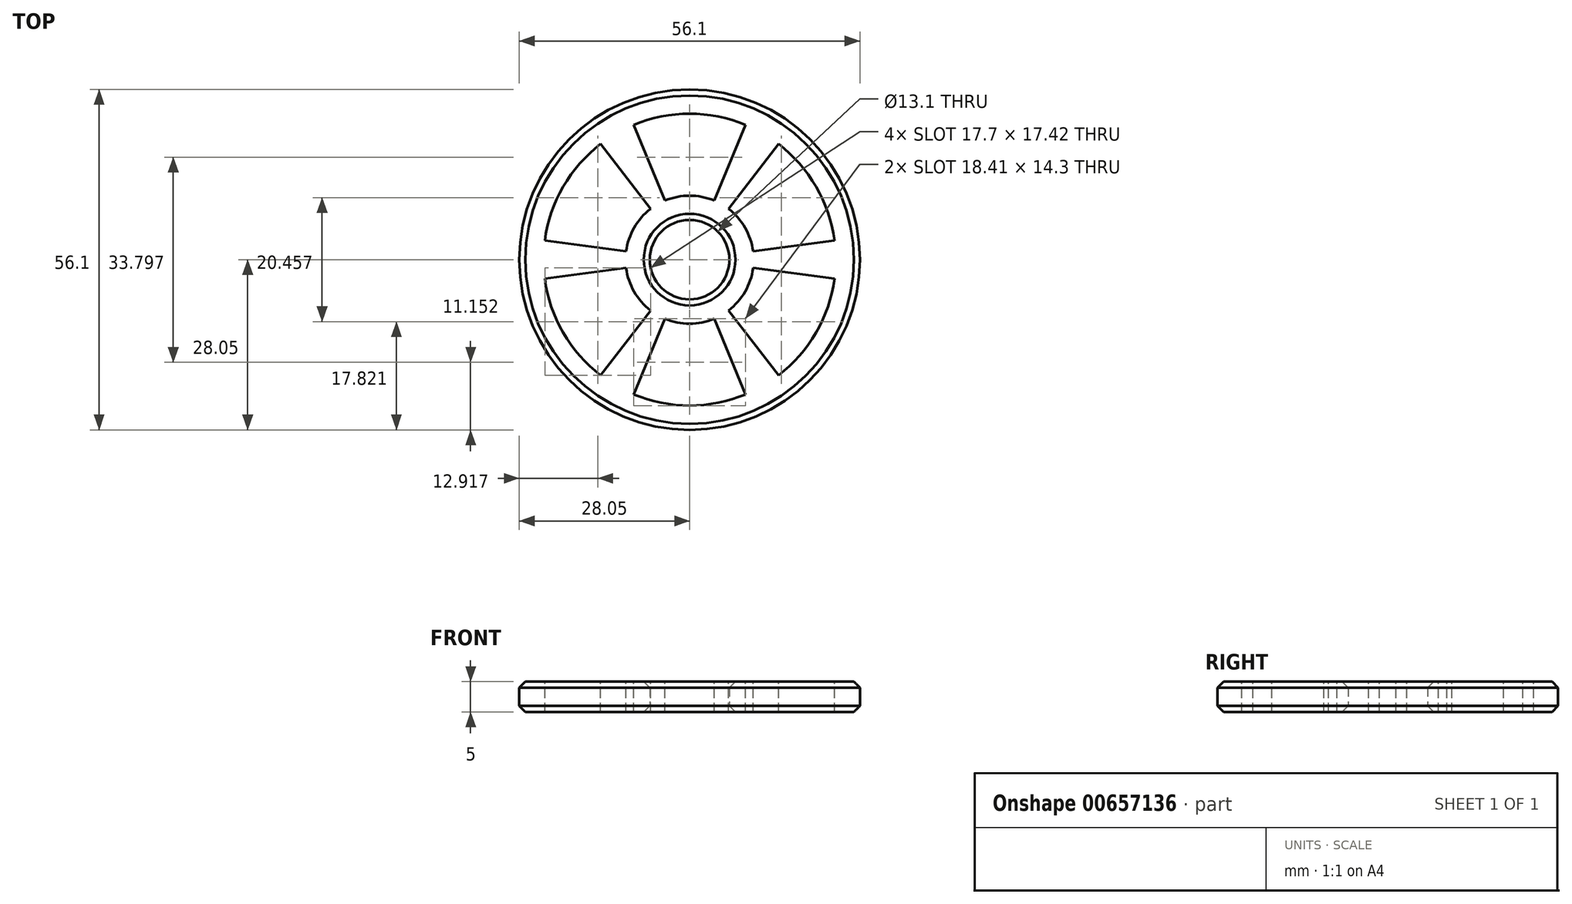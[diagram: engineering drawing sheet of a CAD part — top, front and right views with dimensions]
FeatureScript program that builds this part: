
annotation { "Feature Type Name" : "Feature", "Feature Type Description" : "" }
export const myFeature = defineFeature(function(context is Context, id is Id, definition is map)
    precondition{}
    {
        {
            assignVariable(context, id + "F0", {"name" : "e", "anyValue" : 5});
        }
        {
            var Q0;
            Q0=qCreatedBy(makeId("Top.planeOp"),FACE);
            var sketch = newSketch(context, id + "F1", { "sketchPlane" : qUnion([Q0])});
            skCircle(sketch, "E0", {"center": v(0, 0) * mm, "radius": 28.05 * mm});
            skCircle(sketch, "E1", {"center": v(0, 0) * mm, "radius": 6.55 * mm});
            skSolve(sketch);
        }
        {
            var Q0;
            Q0=makeQuery(id+"F1.imprint","IMPRINT",FACE,{"disambiguationData":[TD([[makeQuery(id+"F1.imprint","IMPRINT",EDGE,{"derivedFrom":sQuery(id+"F1.wireOp",EDGE,"E0")}),1.0]])]});
            extrude(context, id + "F2", {"entities" : qUnion([Q0]), "depth" : (getVariable(context, 'e')) * mm, "offsetDistance" : 25 * mm});
        }
        {
            var Q0;
            Q0=makeQuery(id+"F2.opExtrude","CAP_EDGE",EDGE,{"disambiguationData":[OSD([sQuery(id+"F1.wireOp",EDGE,"E0")])],"isStart":true});
            var Q1;
            Q1=makeQuery(id+"F2.opExtrude","CAP_EDGE",EDGE,{"disambiguationData":[OSD([sQuery(id+"F1.wireOp",EDGE,"E0")])],"isStart":false});
            var Q2;
            Q2=makeQuery(id+"F2.opExtrude","CAP_EDGE",EDGE,{"disambiguationData":[OSD([sQuery(id+"F1.wireOp",EDGE,"E1")])],"isStart":false});
            var Q3;
            Q3=makeQuery(id+"F2.opExtrude","CAP_EDGE",EDGE,{"disambiguationData":[OSD([sQuery(id+"F1.wireOp",EDGE,"E1")])],"isStart":true});
            chamfer(context, id + "F3", {"entities" : qUnion([Q0, Q1, Q2, Q3]), "width" : 1 * mm, "tangentPropagation" : true});
        }
        {
            var Q0;
            Q0=makeQuery(id+"F2.opExtrude","CAP_FACE",FACE,{"disambiguationData":[OSD([sQuery(id+"F1.wireOp",EDGE,"E0"),sQuery(id+"F1.wireOp",EDGE,"E1")])],"isStart":false});
            var sketch = newSketch(context, id + "F4", { "sketchPlane" : qUnion([Q0])});
            skArc(sketch, "E2", {"start": v(9.2, 22.22) * mm, "mid": v(0, 24.05) * mm, "end": v(-9.2, 22.22) * mm});
            skArc(sketch, "E3", {"start": v(4.04, 9.75) * mm, "mid": v(0, 10.55) * mm, "end": v(-4.04, 9.75) * mm});
            skLineSegment(sketch, "E4", {"start": v(-9.2, 22.22) * mm, "end": v(-4.04, 9.75) * mm});
            skLineSegment(sketch, "E5", {"start": v(9.2, 22.22) * mm, "end": v(4.04, 9.75) * mm});
            skLineSegment(sketch, "E6.1.0", {"start": v(-23.84, 3.14) * mm, "end": v(-10.46, 1.38) * mm});
            skArc(sketch, "E6.1.1", {"start": v(-14.64, 19.08) * mm, "mid": v(-20.83, 12.03) * mm, "end": v(-23.84, 3.14) * mm});
            skLineSegment(sketch, "E6.1.2", {"start": v(-14.64, 19.08) * mm, "end": v(-6.42, 8.37) * mm});
            skArc(sketch, "E6.1.3", {"start": v(-6.42, 8.37) * mm, "mid": v(-9.14, 5.28) * mm, "end": v(-10.46, 1.38) * mm});
            skLineSegment(sketch, "E6.2.0", {"start": v(-14.64, -19.08) * mm, "end": v(-6.42, -8.37) * mm});
            skArc(sketch, "E6.2.1", {"start": v(-23.84, -3.14) * mm, "mid": v(-20.83, -12.02) * mm, "end": v(-14.64, -19.08) * mm});
            skLineSegment(sketch, "E6.2.2", {"start": v(-23.84, -3.14) * mm, "end": v(-10.46, -1.38) * mm});
            skArc(sketch, "E6.2.3", {"start": v(-10.46, -1.38) * mm, "mid": v(-9.14, -5.27) * mm, "end": v(-6.42, -8.37) * mm});
            skLineSegment(sketch, "E6.3.0", {"start": v(9.2, -22.22) * mm, "end": v(4.04, -9.75) * mm});
            skArc(sketch, "E6.3.1", {"start": v(-9.2, -22.22) * mm, "mid": v(0, -24.05) * mm, "end": v(9.2, -22.22) * mm});
            skLineSegment(sketch, "E6.3.2", {"start": v(-9.2, -22.22) * mm, "end": v(-4.04, -9.75) * mm});
            skArc(sketch, "E6.3.3", {"start": v(-4.04, -9.75) * mm, "mid": v(0, -10.55) * mm, "end": v(4.04, -9.75) * mm});
            skLineSegment(sketch, "E6.4.0", {"start": v(23.84, -3.14) * mm, "end": v(10.46, -1.38) * mm});
            skArc(sketch, "E6.4.1", {"start": v(14.64, -19.08) * mm, "mid": v(20.83, -12.03) * mm, "end": v(23.84, -3.14) * mm});
            skLineSegment(sketch, "E6.4.2", {"start": v(14.64, -19.08) * mm, "end": v(6.42, -8.37) * mm});
            skArc(sketch, "E6.4.3", {"start": v(6.42, -8.37) * mm, "mid": v(9.14, -5.28) * mm, "end": v(10.46, -1.38) * mm});
            skLineSegment(sketch, "E6.5.0", {"start": v(14.64, 19.08) * mm, "end": v(6.42, 8.37) * mm});
            skArc(sketch, "E6.5.1", {"start": v(23.84, 3.14) * mm, "mid": v(20.83, 12.03) * mm, "end": v(14.64, 19.08) * mm});
            skLineSegment(sketch, "E6.5.2", {"start": v(23.84, 3.14) * mm, "end": v(10.46, 1.38) * mm});
            skArc(sketch, "E6.5.3", {"start": v(10.46, 1.38) * mm, "mid": v(9.14, 5.28) * mm, "end": v(6.42, 8.37) * mm});
            skSolve(sketch);
        }
        {
            var Q0;
            Q0 = qSketchRegion(id + "F4", true);
            extrude(context, id + "F5", {"entities" : qUnion([Q0]), "operationType" : NewBodyOperationType.REMOVE, "endBound" : BoundingType.THROUGH_ALL, "oppositeDirection" : true, "depth" : 25 * mm, "offsetDistance" : 25 * mm});
        }
    });
